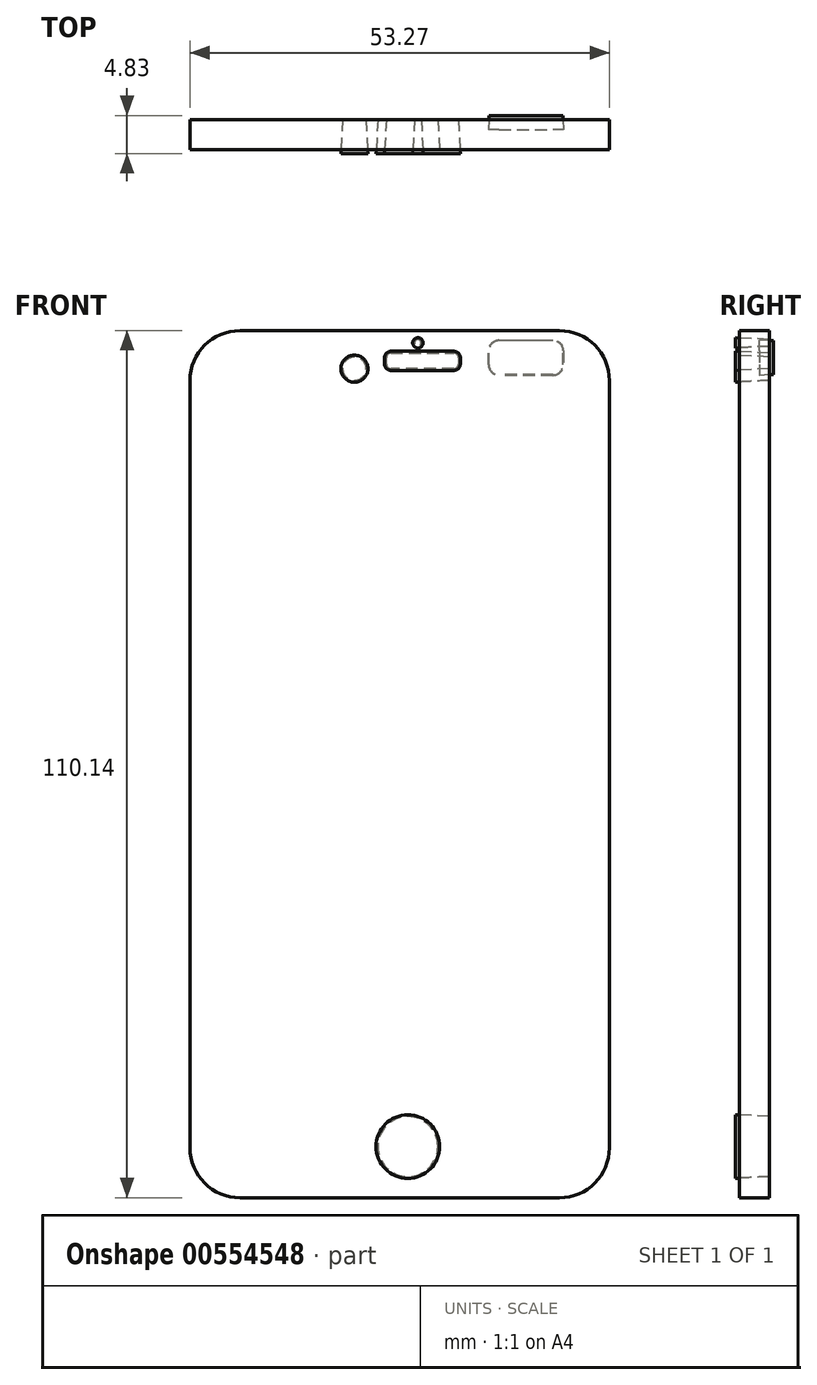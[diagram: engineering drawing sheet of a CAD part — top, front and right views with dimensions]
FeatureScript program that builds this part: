
annotation { "Feature Type Name" : "Feature", "Feature Type Description" : "" }
export const myFeature = defineFeature(function(context is Context, id is Id, definition is map)
    precondition{}
    {
        {
            var Q0;
            Q0=qCreatedBy(makeId("Front.planeOp"),FACE);
            var sketch = newSketch(context, id + "F0", { "sketchPlane" : qUnion([Q0])});
            skLineSegment(sketch, "E0", {"start": v(-22.6, 57.23) * mm, "end": v(13.93, 57.23) * mm});
            skPoint(sketch, "E1.visualSharp", {"position": v(-28.94, 57.23) * mm});
            skArc(sketch, "E1.filletArc", {"start": v(-22.6, 57.23) * mm, "mid": v(-27.08, 55.37) * mm, "end": v(-28.94, 50.88) * mm});
            skLineSegment(sketch, "E2", {"start": v(13.93, 57.23) * mm, "end": v(18.62, 57.23) * mm});
            skLineSegment(sketch, "E3", {"start": v(16.88, 57.23) * mm, "end": v(18.62, 57.23) * mm});
            skLineSegment(sketch, "E4", {"start": v(17.98, 57.23) * mm, "end": v(18.62, 57.23) * mm});
            skPoint(sketch, "E5.visualSharp", {"position": v(24.33, 57.23) * mm});
            skArc(sketch, "E5.filletArc", {"start": v(24.33, 50.88) * mm, "mid": v(22.47, 55.37) * mm, "end": v(17.98, 57.23) * mm});
            skLineSegment(sketch, "E6", {"start": v(-28.94, 50.88) * mm, "end": v(-28.94, -46.56) * mm});
            skLineSegment(sketch, "E7", {"start": v(-22.6, -52.9) * mm, "end": v(17.98, -52.9) * mm});
            skLineSegment(sketch, "E8", {"start": v(24.33, 50.88) * mm, "end": v(24.33, -46.56) * mm});
            skPoint(sketch, "E9.visualSharp", {"position": v(-28.94, -52.9) * mm});
            skArc(sketch, "E9.filletArc", {"start": v(-28.94, -46.56) * mm, "mid": v(-27.08, -51.05) * mm, "end": v(-22.6, -52.9) * mm});
            skPoint(sketch, "E10.newPointA", {"position": v(24.33, -52.9) * mm});
            skPoint(sketch, "E10.newPointB", {"position": v(23.41, -52.9) * mm});
            skArc(sketch, "E10.filletArc", {"start": v(17.98, -52.9) * mm, "mid": v(22.47, -51.05) * mm, "end": v(24.33, -46.56) * mm});
            skSolve(sketch);
        }
        {
            var Q0;
            Q0 = qSketchRegion(id + "F0", true);
            extrude(context, id + "F1", {"entities" : qUnion([Q0]), "depth" : 3.8 * mm, "offsetDistance" : 25.4 * mm});
        }
        {
            var Q0;
            Q0=qCreatedBy(makeId("Front.planeOp"),FACE);
            var sketch = newSketch(context, id + "F2", { "sketchPlane" : qUnion([Q0])});
            skLineSegment(sketch, "E11", {"start": v(0, -39.27) * mm, "end": v(23.97, -39.27) * mm});
            skLineSegment(sketch, "E12", {"start": v(23.97, -39.27) * mm, "end": v(-28.76, -39.27) * mm});
            skLineSegment(sketch, "E13", {"start": v(0, 48.67) * mm, "end": v(-28.58, 48.67) * mm});
            skLineSegment(sketch, "E14", {"start": v(-28.58, 48.67) * mm, "end": v(24.33, 48.67) * mm});
            skCircle(sketch, "E15", {"center": v(-8.06, 52.4) * mm, "radius": 1.49 * mm});
            skLineSegment(sketch, "E16.bottom", {"start": v(-3.42, 54.38) * mm, "end": v(4.58, 54.38) * mm});
            skLineSegment(sketch, "E16.top", {"start": v(-3.42, 52.4) * mm, "end": v(4.58, 52.4) * mm});
            skLineSegment(sketch, "E16.left", {"start": v(-4, 53.8) * mm, "end": v(-4, 52.99) * mm});
            skLineSegment(sketch, "E16.right", {"start": v(5.16, 53.8) * mm, "end": v(5.16, 52.99) * mm});
            skPoint(sketch, "E17.visualSharp", {"position": v(5.16, 54.38) * mm});
            skArc(sketch, "E17.filletArc", {"start": v(5.16, 53.8) * mm, "mid": v(5, 54.21) * mm, "end": v(4.58, 54.38) * mm});
            skPoint(sketch, "E18.visualSharp", {"position": v(5.16, 52.4) * mm});
            skArc(sketch, "E18.filletArc", {"start": v(4.58, 52.4) * mm, "mid": v(5, 52.58) * mm, "end": v(5.16, 52.99) * mm});
            skPoint(sketch, "E19.visualSharp", {"position": v(-4, 54.38) * mm});
            skArc(sketch, "E19.filletArc", {"start": v(-3.42, 54.38) * mm, "mid": v(-3.84, 54.21) * mm, "end": v(-4, 53.8) * mm});
            skPoint(sketch, "E20.visualSharp", {"position": v(-4, 52.4) * mm});
            skArc(sketch, "E20.filletArc", {"start": v(-4, 52.99) * mm, "mid": v(-3.84, 52.58) * mm, "end": v(-3.42, 52.4) * mm});
            skCircle(sketch, "E21", {"center": v(0, 55.68) * mm, "radius": 0.43 * mm});
            skCircle(sketch, "E22", {"center": v(-1.27, -46.42) * mm, "radius": 3.81 * mm});
            skSolve(sketch);
        }
        {
            var Q0;
            Q0 = qSketchRegion(id + "F2", true);
            extrude(context, id + "F3", {"entities" : qUnion([Q0]), "depth" : 4.32 * mm, "offsetDistance" : 25.4 * mm, "hasDraft" : true, "draftAngle" : 3 * degree});
        }
        {
            var Q0;
            Q0=qCreatedBy(makeId("Front.planeOp"),FACE);
            var sketch = newSketch(context, id + "F4", { "sketchPlane" : qUnion([Q0])});
            skLineSegment(sketch, "E23.bottom", {"start": v(17.17, 51.62) * mm, "end": v(10.3, 51.62) * mm});
            skLineSegment(sketch, "E23.top", {"start": v(17.17, 55.95) * mm, "end": v(10.3, 55.95) * mm});
            skLineSegment(sketch, "E23.left", {"start": v(18.44, 52.89) * mm, "end": v(18.44, 54.68) * mm});
            skLineSegment(sketch, "E23.right", {"start": v(9.03, 52.89) * mm, "end": v(9.03, 54.68) * mm});
            skPoint(sketch, "E24.visualSharp", {"position": v(9.03, 55.95) * mm});
            skArc(sketch, "E24.filletArc", {"start": v(10.3, 55.95) * mm, "mid": v(9.4, 55.58) * mm, "end": v(9.03, 54.68) * mm});
            skPoint(sketch, "E25.visualSharp", {"position": v(18.44, 55.95) * mm});
            skArc(sketch, "E25.filletArc", {"start": v(18.44, 54.68) * mm, "mid": v(18.06, 55.58) * mm, "end": v(17.17, 55.95) * mm});
            skPoint(sketch, "E26.visualSharp", {"position": v(18.44, 51.62) * mm});
            skArc(sketch, "E26.filletArc", {"start": v(17.17, 51.62) * mm, "mid": v(18.06, 52) * mm, "end": v(18.44, 52.89) * mm});
            skPoint(sketch, "E27.visualSharp", {"position": v(9.03, 51.62) * mm});
            skArc(sketch, "E27.filletArc", {"start": v(9.03, 52.89) * mm, "mid": v(9.4, 52) * mm, "end": v(10.3, 51.62) * mm});
            skSolve(sketch);
        }
        {
            var Q0;
            Q0 = qSketchRegion(id + "F4", true);
            extrude(context, id + "F5", {"entities" : qUnion([Q0]), "depth" : 1.27 * mm, "offsetDistance" : 25.4 * mm, "hasDraft" : true, "draftAngle" : 3 * degree, "hasSecondDirection" : true, "secondDirectionOppositeDirection" : true, "secondDirectionDepth" : 0.5 * mm});
        }
    });
